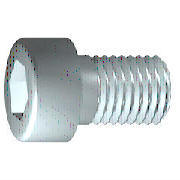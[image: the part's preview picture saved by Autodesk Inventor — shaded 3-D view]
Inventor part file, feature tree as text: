
AUTODESK INVENTOR PART (.ipt)
format: ipt  version: 2014 (Build 180170000, 170)  size: 192,000 bytes
history: native  units: mm (DEFAULTED — no unit token found)
features: sketch x2, extrude x1, plane x1, fillet x1
ambient origin geometry x7: Origin, YZ Plane, XY Plane, X Axis, Y Axis, Z Axis, Center Point
bodies: Solid1 (feature_tree), Body (feature_tree)
feature tree (5):
  extrude  "Slot"  Depth=4.826mm
  plane  "Work Plane1"
  fillet  "Fillet2"  Radius=4.826mm
  sketch  "Sketch1"  dims[d1=14.684048mm d2=1.190852mm d3=4.826mm]
  sketch  "Sketch2"  dims[d4=2.286mm d5=60.0deg d6=4.826mm d7=4.826mm d8=4.575385mm d9=7.9248mm d10=90.0deg d11=10.0mm d12=0.0mm d13=14.684048mm d14=0.0mm d15=0.47244mm d16=0.47244mm d17=0.4572mm d19=0.0mm d26=15.875mm d27=45.0deg d28=0.0mm d29=0.0mm d30=0.1524mm]
